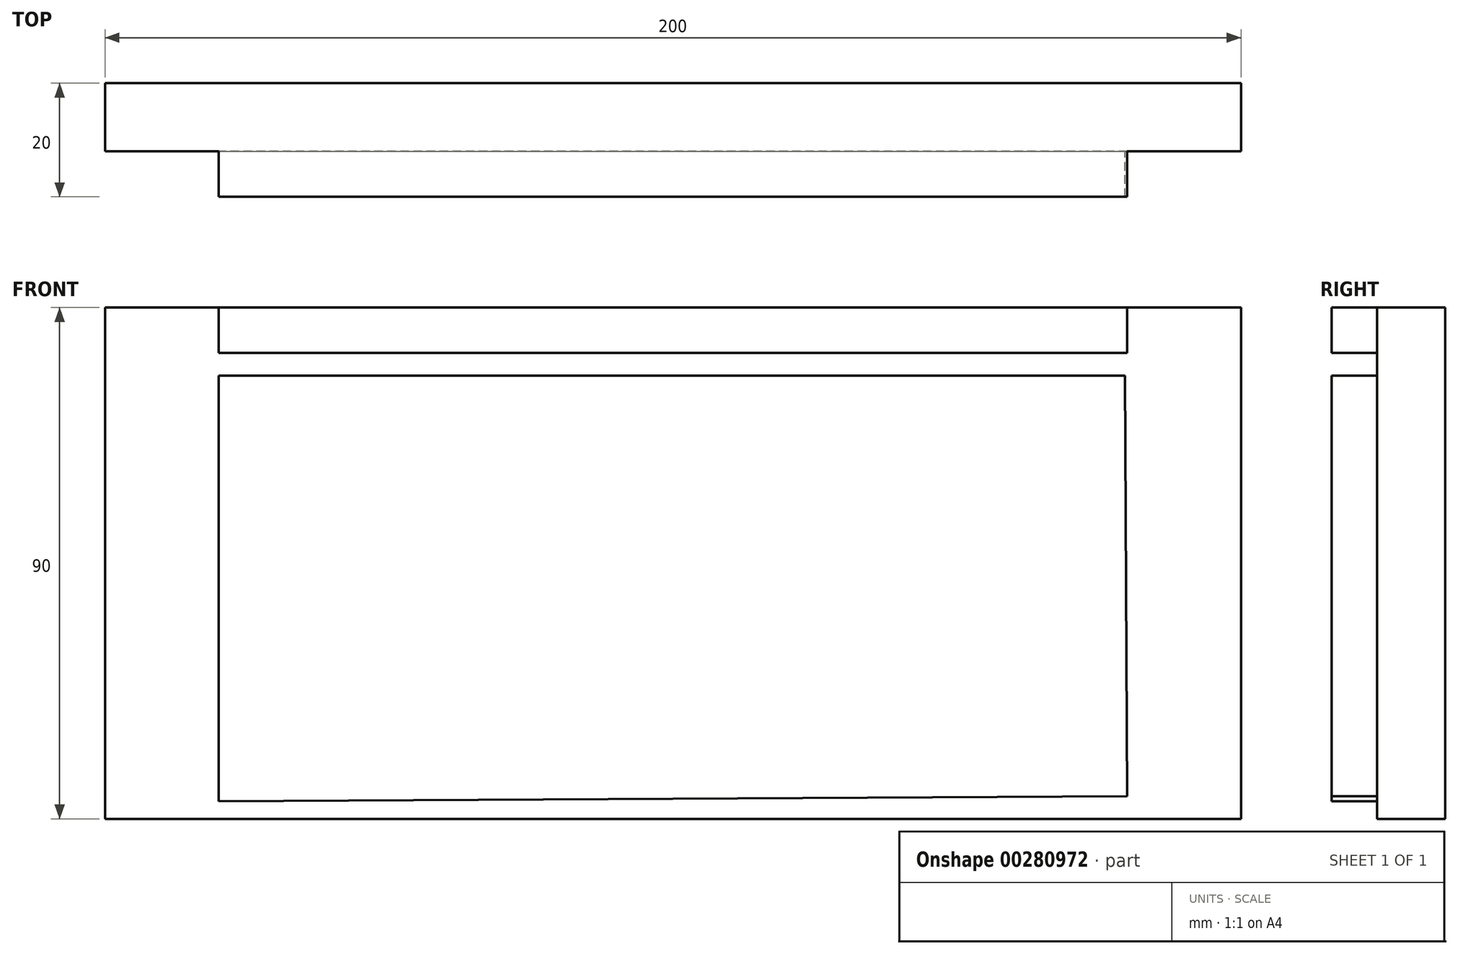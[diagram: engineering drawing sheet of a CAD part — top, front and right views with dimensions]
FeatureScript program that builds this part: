
annotation { "Feature Type Name" : "Feature", "Feature Type Description" : "" }
export const myFeature = defineFeature(function(context is Context, id is Id, definition is map)
    precondition{}
    {
        {
            var Q0;
            Q0=qCreatedBy(makeId("Front.planeOp"),FACE);
            var sketch = newSketch(context, id + "F0", { "sketchPlane" : qUnion([Q0])});
            skLineSegment(sketch, "E0", {"start": v(-65.9, -14.65) * mm, "end": v(94.1, -14.65) * mm});
            skLineSegment(sketch, "E1", {"start": v(-85.9, 75.35) * mm, "end": v(-85.9, -14.65) * mm});
            skLineSegment(sketch, "E2", {"start": v(-85.9, -14.65) * mm, "end": v(114.1, -14.65) * mm});
            skLineSegment(sketch, "E3", {"start": v(114.1, -14.65) * mm, "end": v(114.1, 75.35) * mm});
            skLineSegment(sketch, "E4", {"start": v(-65.9, 75.35) * mm, "end": v(-85.9, 75.35) * mm});
            skLineSegment(sketch, "E5", {"start": v(94.1, 75.35) * mm, "end": v(114.1, 75.35) * mm});
            skLineSegment(sketch, "E6", {"start": v(-65.9, 75.35) * mm, "end": v(-65.9, 67.35) * mm});
            skLineSegment(sketch, "E7", {"start": v(-65.9, 67.35) * mm, "end": v(94.1, 67.35) * mm});
            skLineSegment(sketch, "E8", {"start": v(94.1, 67.35) * mm, "end": v(94.1, 75.35) * mm});
            skLineSegment(sketch, "E9", {"start": v(-65.9, -14.65) * mm, "end": v(-65.9, 63.35) * mm});
            skLineSegment(sketch, "E10", {"start": v(93.66, 63.35) * mm, "end": v(94.1, -14.65) * mm});
            skLineSegment(sketch, "E11", {"start": v(93.66, 63.35) * mm, "end": v(-65.9, 63.35) * mm});
            skLineSegment(sketch, "E12", {"start": v(-65.9, 75.35) * mm, "end": v(94.1, 75.35) * mm});
            skSolve(sketch);
        }
        {
            var Q0;
            Q0 = qSketchRegion(id + "F0", true);
            extrude(context, id + "F1", {"entities" : qUnion([Q0]), "depth" : 12 * mm});
        }
        {
            var Q0;
            Q0=makeQuery(id+"F0.imprint","IMPRINT",FACE,{"disambiguationData":[TD([[makeQuery(id+"F0.imprint","IMPRINT",EDGE,{"derivedFrom":sQuery(id+"F0.wireOp",EDGE,"E6")}),1.0]])]});
            var Q1;
            {var subQ0=sQuery(id+"F0.wireOp",EDGE,"E9");Q1=makeQuery(id+"F0.imprint","IMPRINT",FACE,{"disambiguationData":[TD([[makeQuery(id+"F0.imprint","IMPRINT",EDGE,{"derivedFrom":subQ0}),-1.0]])]});}
            extrude(context, id + "F2", {"entities" : qUnion([Q0, Q1]), "operationType" : NewBodyOperationType.ADD, "depth" : 20 * mm});
        }
        {
            var Q0;
            Q0=makeQuery(id+"F2.opExtrude","SWEPT_FACE",FACE,{"disambiguationData":[OSD([sQuery(id+"F0.wireOp",EDGE,"E10")])]});
            var sketch = newSketch(context, id + "F3", { "sketchPlane" : qUnion([Q0])});
            skLineSegment(sketch, "E13.bottom", {"start": v(-20, -15.18) * mm, "end": v(-12, -15.18) * mm});
            skLineSegment(sketch, "E13.top", {"start": v(-20, -11.18) * mm, "end": v(-12, -11.18) * mm});
            skLineSegment(sketch, "E13.left", {"start": v(-20, -15.18) * mm, "end": v(-20, -11.18) * mm});
            skLineSegment(sketch, "E13.right", {"start": v(-12, -15.18) * mm, "end": v(-12, -11.18) * mm});
            skSolve(sketch);
        }
        {
            var Q0;
            Q0=makeQuery(id+"F3.imprint","IMPRINT",FACE,{"disambiguationData":[TD([[makeQuery(id+"F3.imprint","IMPRINT",EDGE,{"derivedFrom":sQuery(id+"F3.wireOp",EDGE,"E13.bottom")}),1.0]])]});
            extrude(context, id + "F4", {"entities" : qUnion([Q0]), "operationType" : NewBodyOperationType.REMOVE, "endBound" : BoundingType.UP_TO_NEXT, "oppositeDirection" : true, "depth" : 25 * mm});
        }
    });
